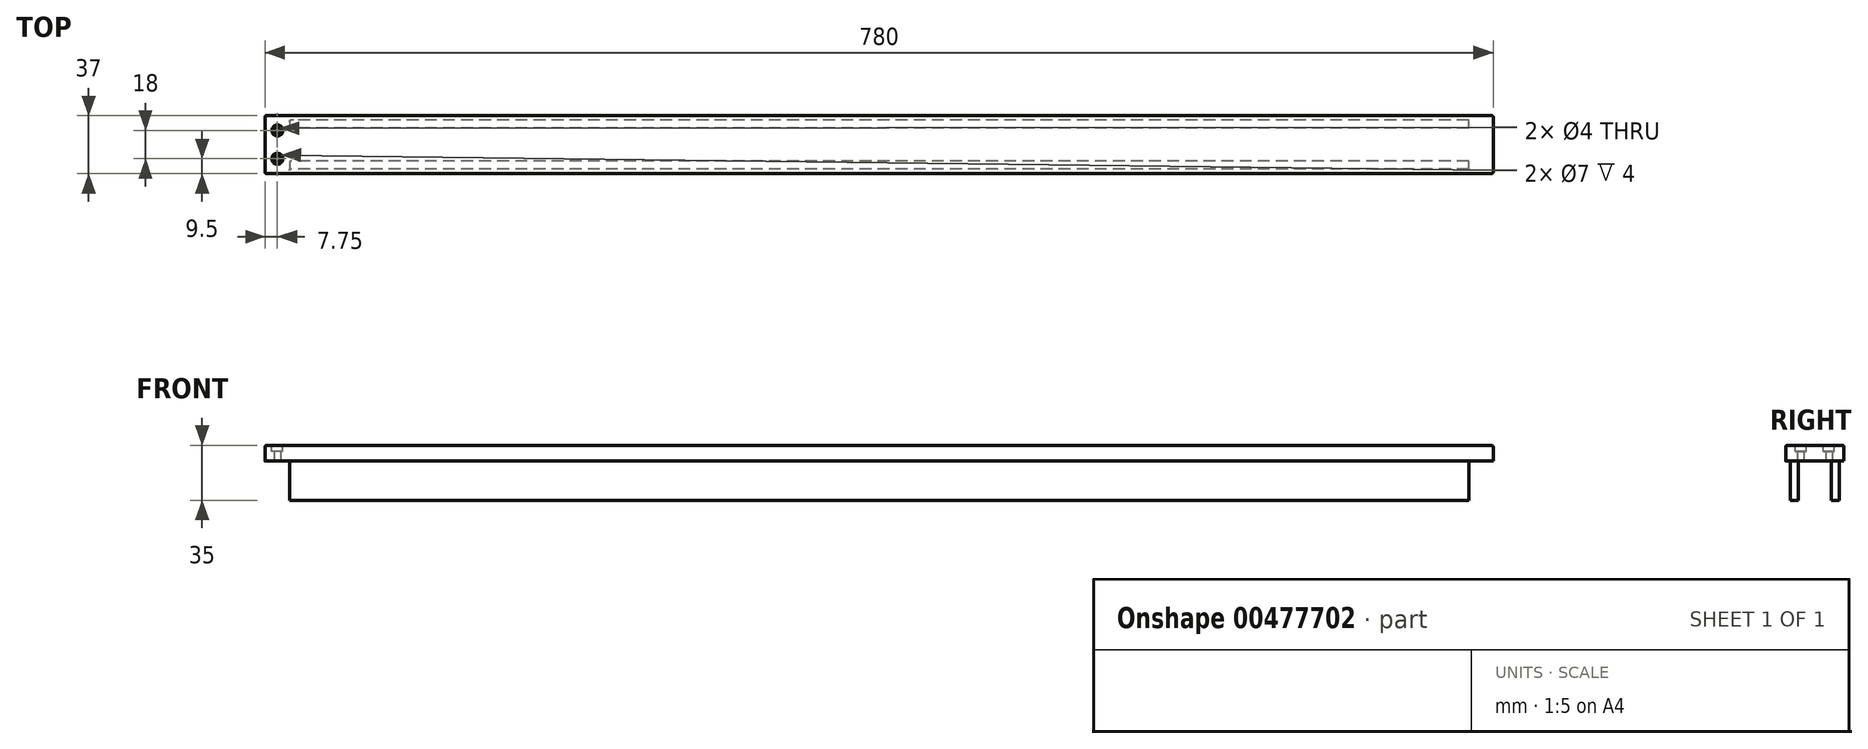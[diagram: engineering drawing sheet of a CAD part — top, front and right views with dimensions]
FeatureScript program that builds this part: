
annotation { "Feature Type Name" : "Feature", "Feature Type Description" : "" }
export const myFeature = defineFeature(function(context is Context, id is Id, definition is map)
    precondition{}
    {
        {
            var Q0;
            Q0=qCreatedBy(makeId("Right.planeOp"),FACE);
            var sketch = newSketch(context, id + "F0", { "sketchPlane" : qUnion([Q0])});
            skLineSegment(sketch, "E0", {"start": v(0, 60.8) * mm, "end": v(0, -55.58) * mm, "construction": true});
            skLineSegment(sketch, "E1", {"start": v(66.15, 0) * mm, "end": v(-54.47, 0) * mm, "construction": true});
            skLineSegment(sketch, "E2.bottom", {"start": v(-18.5, 12.5) * mm, "end": v(18.5, 12.5) * mm});
            skLineSegment(sketch, "E2.top", {"start": v(-15.5, -22.5) * mm, "end": v(-10.5, -22.5) * mm});
            skLineSegment(sketch, "E2.left", {"start": v(-18.5, 12.5) * mm, "end": v(-18.5, 2.5) * mm});
            skLineSegment(sketch, "E2.right", {"start": v(18.5, 12.5) * mm, "end": v(18.5, 0) * mm, "construction": true});
            skLineSegment(sketch, "E3", {"start": v(-18.5, 2.5) * mm, "end": v(-15.5, 2.5) * mm});
            skLineSegment(sketch, "E4", {"start": v(-15.5, 2.5) * mm, "end": v(-15.5, -22.5) * mm});
            skLineSegment(sketch, "E5", {"start": v(-10.5, -22.5) * mm, "end": v(-10.5, 2.5) * mm});
            skLineSegment(sketch, "E6", {"start": v(-10.5, 2.5) * mm, "end": v(0, 2.5) * mm});
            skLineSegment(sketch, "E7.MirrorCS", {"start": v(10.5, 2.5) * mm, "end": v(0, 2.5) * mm});
            skLineSegment(sketch, "E8.MirrorCS", {"start": v(10.5, -22.5) * mm, "end": v(10.5, 2.5) * mm});
            skLineSegment(sketch, "E9.MirrorCS", {"start": v(15.5, 2.5) * mm, "end": v(15.5, -22.5) * mm});
            skLineSegment(sketch, "E10.MirrorCS", {"start": v(15.5, -22.5) * mm, "end": v(10.5, -22.5) * mm});
            skLineSegment(sketch, "E11.MirrorCS", {"start": v(18.5, 2.5) * mm, "end": v(15.5, 2.5) * mm});
            skLineSegment(sketch, "E12", {"start": v(18.5, 2.5) * mm, "end": v(18.5, 12.5) * mm});
            skSolve(sketch);
        }
        {
            var Q0;
            Q0 = qSketchRegion(id + "F0", true);
            extrude(context, id + "F1", {"entities" : qUnion([Q0]), "depth" : 780 * mm, "symmetric" : true});
        }
        {
            var Q0;
            Q0=makeQuery(id+"F1.opExtrude","CAP_FACE",FACE,{"disambiguationData":[OSD([sQuery(id+"F0.wireOp",EDGE,"E2.bottom"),sQuery(id+"F0.wireOp",EDGE,"E2.top"),sQuery(id+"F0.wireOp",EDGE,"E2.left"),sQuery(id+"F0.wireOp",EDGE,"E3"),sQuery(id+"F0.wireOp",EDGE,"E4"),sQuery(id+"F0.wireOp",EDGE,"E5"),sQuery(id+"F0.wireOp",EDGE,"E6"),sQuery(id+"F0.wireOp",EDGE,"E7.MirrorCS"),sQuery(id+"F0.wireOp",EDGE,"E8.MirrorCS"),sQuery(id+"F0.wireOp",EDGE,"E9.MirrorCS"),sQuery(id+"F0.wireOp",EDGE,"E10.MirrorCS"),sQuery(id+"F0.wireOp",EDGE,"E11.MirrorCS"),sQuery(id+"F0.wireOp",EDGE,"E12")])],"isStart":true});
            var sketch = newSketch(context, id + "F2", { "sketchPlane" : qUnion([Q0])});
            skLineSegment(sketch, "E13.bottom", {"start": v(-15.5, 2.5) * mm, "end": v(15.5, 2.5) * mm});
            skLineSegment(sketch, "E13.top", {"start": v(-15.5, -22.5) * mm, "end": v(15.5, -22.5) * mm});
            skLineSegment(sketch, "E13.left", {"start": v(-15.5, 2.5) * mm, "end": v(-15.5, -22.5) * mm});
            skLineSegment(sketch, "E13.right", {"start": v(15.5, 2.5) * mm, "end": v(15.5, -22.5) * mm});
            skSolve(sketch);
        }
        {
            var Q0;
            Q0 = qSketchRegion(id + "F2", true);
            extrude(context, id + "F3", {"entities" : qUnion([Q0]), "operationType" : NewBodyOperationType.REMOVE, "oppositeDirection" : true, "depth" : 15.5 * mm});
        }
        {
            var Q0;
            Q0=makeQuery(id+"F1.opExtrude","CAP_FACE",FACE,{"disambiguationData":[OSD([sQuery(id+"F0.wireOp",EDGE,"E2.bottom"),sQuery(id+"F0.wireOp",EDGE,"E2.top"),sQuery(id+"F0.wireOp",EDGE,"E2.left"),sQuery(id+"F0.wireOp",EDGE,"E3"),sQuery(id+"F0.wireOp",EDGE,"E4"),sQuery(id+"F0.wireOp",EDGE,"E5"),sQuery(id+"F0.wireOp",EDGE,"E6"),sQuery(id+"F0.wireOp",EDGE,"E7.MirrorCS"),sQuery(id+"F0.wireOp",EDGE,"E8.MirrorCS"),sQuery(id+"F0.wireOp",EDGE,"E9.MirrorCS"),sQuery(id+"F0.wireOp",EDGE,"E10.MirrorCS"),sQuery(id+"F0.wireOp",EDGE,"E11.MirrorCS"),sQuery(id+"F0.wireOp",EDGE,"E12")])],"isStart":false});
            var sketch = newSketch(context, id + "F4", { "sketchPlane" : qUnion([Q0])});
            skLineSegment(sketch, "E14.bottom", {"start": v(-15.5, 2.5) * mm, "end": v(15.5, 2.5) * mm});
            skLineSegment(sketch, "E14.top", {"start": v(-15.5, -22.5) * mm, "end": v(15.5, -22.5) * mm});
            skLineSegment(sketch, "E14.left", {"start": v(-15.5, 2.5) * mm, "end": v(-15.5, -22.5) * mm});
            skLineSegment(sketch, "E14.right", {"start": v(15.5, 2.5) * mm, "end": v(15.5, -22.5) * mm});
            skSolve(sketch);
        }
        {
            var Q0;
            Q0 = qSketchRegion(id + "F4", true);
            extrude(context, id + "F5", {"entities" : qUnion([Q0]), "operationType" : NewBodyOperationType.REMOVE, "oppositeDirection" : true, "depth" : 15.5 * mm});
        }
        {
            var Q0;
            Q0=makeQuery(id+"F5.boolean.opBoolean","MERGE",FACE,{"derivedFrom":[makeQuery(id+"F3.boolean.opBoolean","MERGE",FACE,{"derivedFrom":[makeQuery(id+"F1.opExtrude","SWEPT_FACE",FACE,{"disambiguationData":[OSD([sQuery(id+"F0.wireOp",EDGE,"E3")])]}),makeQuery(id+"F1.opExtrude","SWEPT_FACE",FACE,{"disambiguationData":[OSD([sQuery(id+"F0.wireOp",EDGE,"E6"),sQuery(id+"F0.wireOp",EDGE,"E7.MirrorCS")])]}),makeQuery(id+"F1.opExtrude","SWEPT_FACE",FACE,{"disambiguationData":[OSD([sQuery(id+"F0.wireOp",EDGE,"E11.MirrorCS")])]}),makeQuery(id+"F3.opExtrude","SWEPT_FACE",FACE,{"disambiguationData":[OSD([sQuery(id+"F2.wireOp",EDGE,"E13.bottom")])]})]}),makeQuery(id+"F5.opExtrude","SWEPT_FACE",FACE,{"disambiguationData":[OSD([sQuery(id+"F4.wireOp",EDGE,"E14.bottom")])]})]});
            var sketch = newSketch(context, id + "F6", { "sketchPlane" : qUnion([Q0])});
            skLineSegment(sketch, "E15", {"start": v(-374.5, 15.5) * mm, "end": v(-374.5, -15.5) * mm, "construction": true});
            skLineSegment(sketch, "E16", {"start": v(-374.5, 0) * mm, "end": v(-390, 0) * mm, "construction": true});
            skLineSegment(sketch, "E17", {"start": v(-382.25, 0) * mm, "end": v(-382.25, 18.5) * mm, "construction": true});
            skCircle(sketch, "E18", {"center": v(-382.25, 9) * mm, "radius": 2 * mm});
            skCircle(sketch, "E19.MirrorC", {"center": v(-382.25, -9) * mm, "radius": 2 * mm});
            skSolve(sketch);
        }
        {
            var Q0;
            Q0 = qSketchRegion(id + "F6", true);
            extrude(context, id + "F7", {"entities" : qUnion([Q0]), "operationType" : NewBodyOperationType.REMOVE, "endBound" : BoundingType.THROUGH_ALL, "oppositeDirection" : true, "depth" : 25 * mm});
        }
        {
            var Q0;
            Q0=makeQuery(id+"F1.opExtrude","SWEPT_FACE",FACE,{"disambiguationData":[OSD([sQuery(id+"F0.wireOp",EDGE,"E2.bottom")])]});
            var sketch = newSketch(context, id + "F8", { "sketchPlane" : qUnion([Q0])});
            skCircle(sketch, "E20.0", {"center": v(-382.25, -9) * mm, "radius": 3.5 * mm});
            skCircle(sketch, "E21.0", {"center": v(-382.25, 9) * mm, "radius": 3.5 * mm});
            skLineSegment(sketch, "E22", {"start": v(-385.75, -9) * mm, "end": v(-390, -9) * mm, "construction": true});
            skSolve(sketch);
        }
        {
            var Q0;
            Q0 = qSketchRegion(id + "F8", true);
            extrude(context, id + "F9", {"entities" : qUnion([Q0]), "operationType" : NewBodyOperationType.REMOVE, "oppositeDirection" : true, "depth" : 4 * mm});
        }
        {
            var Q0;
            Q0=makeQuery(id+"F1.opExtrude","CAP_EDGE",EDGE,{"disambiguationData":[OSD([sQuery(id+"F0.wireOp",EDGE,"E12")])],"isStart":false});
            var Q1;
            Q1=makeQuery(id+"F1.opExtrude","CAP_EDGE",EDGE,{"disambiguationData":[OSD([sQuery(id+"F0.wireOp",EDGE,"E2.left")])],"isStart":false});
            var Q2;
            {var subQ0=sQuery(id+"F4.wireOp",EDGE,"E14.top");Q2=makeQuery(id+"F5.boolean.opBoolean","COPY",EDGE,{"disambiguationData":[topologyDisambiguationEdgeConnected([makeQuery(id+"F1.opExtrude","SWEPT_FACE",FACE,{"disambiguationData":[OSD([sQuery(id+"F0.wireOp",EDGE,"E10.MirrorCS")])]})])],"derivedFrom":makeQuery(id+"F5.opExtrude","CAP_EDGE",EDGE,{"disambiguationData":[OSD([subQ0])],"isStart":false})});}
            var Q3;
            {var subQ0=sQuery(id+"F4.wireOp",EDGE,"E14.top");Q3=makeQuery(id+"F5.boolean.opBoolean","COPY",EDGE,{"disambiguationData":[topologyDisambiguationEdgeConnected([makeQuery(id+"F1.opExtrude","SWEPT_FACE",FACE,{"disambiguationData":[OSD([sQuery(id+"F0.wireOp",EDGE,"E2.top")])]})])],"derivedFrom":makeQuery(id+"F5.opExtrude","CAP_EDGE",EDGE,{"disambiguationData":[OSD([subQ0])],"isStart":false})});}
            var Q4;
            Q4=makeQuery(id+"F1.opExtrude","CAP_EDGE",EDGE,{"disambiguationData":[OSD([sQuery(id+"F0.wireOp",EDGE,"E2.left")])],"isStart":true});
            var Q5;
            {var subQ0=sQuery(id+"F2.wireOp",EDGE,"E13.top");Q5=makeQuery(id+"F3.boolean.opBoolean","COPY",EDGE,{"disambiguationData":[topologyDisambiguationEdgeConnected([makeQuery(id+"F1.opExtrude","SWEPT_FACE",FACE,{"disambiguationData":[OSD([sQuery(id+"F0.wireOp",EDGE,"E2.top")])]})])],"derivedFrom":makeQuery(id+"F3.opExtrude","CAP_EDGE",EDGE,{"disambiguationData":[OSD([subQ0])],"isStart":false})});}
            var Q6;
            {var subQ0=sQuery(id+"F2.wireOp",EDGE,"E13.top");Q6=makeQuery(id+"F3.boolean.opBoolean","COPY",EDGE,{"disambiguationData":[topologyDisambiguationEdgeConnected([makeQuery(id+"F1.opExtrude","SWEPT_FACE",FACE,{"disambiguationData":[OSD([sQuery(id+"F0.wireOp",EDGE,"E10.MirrorCS")])]})])],"derivedFrom":makeQuery(id+"F3.opExtrude","CAP_EDGE",EDGE,{"disambiguationData":[OSD([subQ0])],"isStart":false})});}
            var Q7;
            Q7=makeQuery(id+"F1.opExtrude","CAP_EDGE",EDGE,{"disambiguationData":[OSD([sQuery(id+"F0.wireOp",EDGE,"E12")])],"isStart":true});
            fillet(context, id + "F10", {"entities" : qUnion([Q0, Q1, Q2, Q3, Q4, Q5, Q6, Q7]), "radius" : 1 * mm, "tangentPropagation" : true, "allowEdgeOverflow" : false});
        }
        {
            var Q0;
            Q0=makeQuery(id+"F3.boolean.opBoolean","INTERSECT",EDGE,{"derivedFrom":[makeQuery(id+"F1.opExtrude","SWEPT_FACE",FACE,{"disambiguationData":[OSD([sQuery(id+"F0.wireOp",EDGE,"E5")])]}),makeQuery(id+"F3.opExtrude","CAP_FACE",FACE,{"disambiguationData":[OSD([sQuery(id+"F2.wireOp",EDGE,"E13.bottom"),sQuery(id+"F2.wireOp",EDGE,"E13.top"),sQuery(id+"F2.wireOp",EDGE,"E13.left"),sQuery(id+"F2.wireOp",EDGE,"E13.right")])],"isStart":false})]});
            var Q1;
            Q1=makeQuery(id+"F3.boolean.opBoolean","COPY",EDGE,{"derivedFrom":makeQuery(id+"F3.opExtrude","CAP_EDGE",EDGE,{"disambiguationData":[OSD([sQuery(id+"F2.wireOp",EDGE,"E13.right")])],"isStart":false})});
            var Q2;
            Q2=makeQuery(id+"F3.boolean.opBoolean","COPY",EDGE,{"derivedFrom":makeQuery(id+"F3.opExtrude","CAP_EDGE",EDGE,{"disambiguationData":[OSD([sQuery(id+"F2.wireOp",EDGE,"E13.left")])],"isStart":false})});
            var Q3;
            {var subQ0=sQuery(id+"F2.wireOp",EDGE,"E13.bottom");Q3=makeQuery(id+"F3.boolean.opBoolean","COPY",FACE,{"disambiguationData":[TD([makeQuery(id+"F1.opExtrude","SWEPT_FACE",FACE,{"disambiguationData":[OSD([sQuery(id+"F0.wireOp",EDGE,"E8.MirrorCS")])]})])],"derivedFrom":makeQuery(id+"F3.opExtrude","CAP_FACE",FACE,{"disambiguationData":[OSD([subQ0,sQuery(id+"F2.wireOp",EDGE,"E13.top"),sQuery(id+"F2.wireOp",EDGE,"E13.left"),sQuery(id+"F2.wireOp",EDGE,"E13.right")])],"isStart":false})});}
            var Q4;
            Q4=makeQuery(id+"F3.boolean.opBoolean","MERGE",EDGE,{"derivedFrom":[makeQuery(id+"F1.opExtrude","CAP_EDGE",EDGE,{"disambiguationData":[OSD([sQuery(id+"F0.wireOp",EDGE,"E3")])],"isStart":true}),makeQuery(id+"F1.opExtrude","CAP_EDGE",EDGE,{"disambiguationData":[OSD([sQuery(id+"F0.wireOp",EDGE,"E6"),sQuery(id+"F0.wireOp",EDGE,"E7.MirrorCS")])],"isStart":true}),makeQuery(id+"F1.opExtrude","CAP_EDGE",EDGE,{"disambiguationData":[OSD([sQuery(id+"F0.wireOp",EDGE,"E11.MirrorCS")])],"isStart":true}),makeQuery(id+"F3.opExtrude","CAP_EDGE",EDGE,{"disambiguationData":[OSD([sQuery(id+"F2.wireOp",EDGE,"E13.bottom")])],"isStart":true})]});
            var Q5;
            Q5=makeQuery(id+"F1.opExtrude","CAP_EDGE",EDGE,{"disambiguationData":[OSD([sQuery(id+"F0.wireOp",EDGE,"E2.bottom")])],"isStart":true});
            var Q6;
            Q6=makeQuery(id+"F1.opExtrude","SWEPT_EDGE",EDGE,{"disambiguationData":[OSD([sQuery(id+"F0.wireOp",EDGE,"E3"),sQuery(id+"F0.wireOp",EDGE,"E4")])]});
            fillet(context, id + "F11", {"entities" : qUnion([Q0, Q1, Q2, Q3, Q4, Q5, Q6]), "radius" : 1 * mm, "tangentPropagation" : true, "allowEdgeOverflow" : false});
        }
    });
